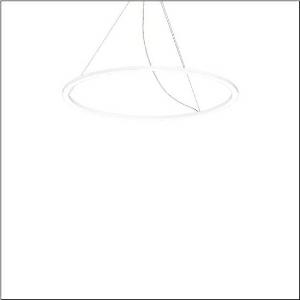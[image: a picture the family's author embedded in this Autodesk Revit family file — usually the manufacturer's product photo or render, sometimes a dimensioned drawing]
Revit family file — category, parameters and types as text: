
# Revit family: silica_21_ring-d_5pjbd3d1004a
name_source: partatom
category: Lighting Fixtures
units: mm (PartAtom-declared; Revit-internal decimal feet)

## family parameters
Cut with Voids When Loaded = No
Host = Face
Light Source = No
Part Type = Normal
Room Calculation Point = No
Round Connector Dimension = Use Diameter
Shared = No

## types (1)
- Silica 21 Ring-D (1 x LED, 8050 lm, 94 W, 3000K)
    Apparent Load = 94 VA
    CIE Flux Codes = 37 69 92 100 100
    Color Rendering = 80
    Color Temperature = 3000K
    Default Elevation = 1800 mm
    Description = Silica® 21 Ring-D, suspended luminaire, of PMMA, frosted, light emission: ring underside luminous distribution, primary light characteristic: symmetric, installation type: suspended mounting, LED, rated luminous flux: 8.050lm, luminous efficacy: 86lm/W, light colour: 830, colour temperature: 3000K, control gear: DALI 2, with terminal, 5-pole, mains connection: 230V, AC/DC, 0/50..60Hz, rated input power: 94W, housing, of extruded aluminium section, traffic white (RAL 9016), diameter: 1.100mm, ceiling canopy, traffic white (RAL 9016), protection rating (lamp compartment): IP40, insulation class (complete): insulation class I (protective earthing), certification: CE, impact resistance: IK02, permissible operating ambient temperature: 0..+35°C, packaging unit: 1 piece
    Height = 25 mm  [stored 0.082021 ft]
    Lamp = 1 x LED
    Lamp Light Flux = 8050 lm
    Lamp Power = 94 W
    Lamp count = 1
    Length = 1100 mm
    Luminous efficacy = 86 lm/W
    Manufacturer = Siteco
    ModVariant = No
    Model = 5PJBD3D1004A
    Mounting Place = Ceiling
    Mounting Type = Pendant
    Number of Poles = 1
    OnlyDefault = Yes
    Power Factor = 1
    Product Name = Silica 21 Ring-D
    Product group = suspended luminaire
    ProductGroupID = 904
    Protection Class = Protection class I
    Protection Degree = IP 40
    RLX_Detail_Level = 1
    RLX_Emergency_Light_Flux = 0 lm
    RLX_Emergency_Type = 0
    RLX_Emergency_Type_DB = No
    RlxData = <blob elided: 12501 chars, md5=97b4ba98>
    Socket = socket
    Standby Power = 0 W
    System Light Flux = 8050 lm
    System Power = 94 W
    Type Comments = Product without accessories
    Type Image = l_1258355.jpg
    URL = http://relux.com
    VarID = ---
    Voltage = 0 V
    Weight = 0.00 kg
    Width = 0 mm  [stored 0 ft]

note: [stored X ft] marks values corroborated as IEEE doubles in the binary element streams (Revit-internal decimal feet)

## geometry (parser evidence)
native form markers: Sweep x10
no freeform markers — native parametric forms only
